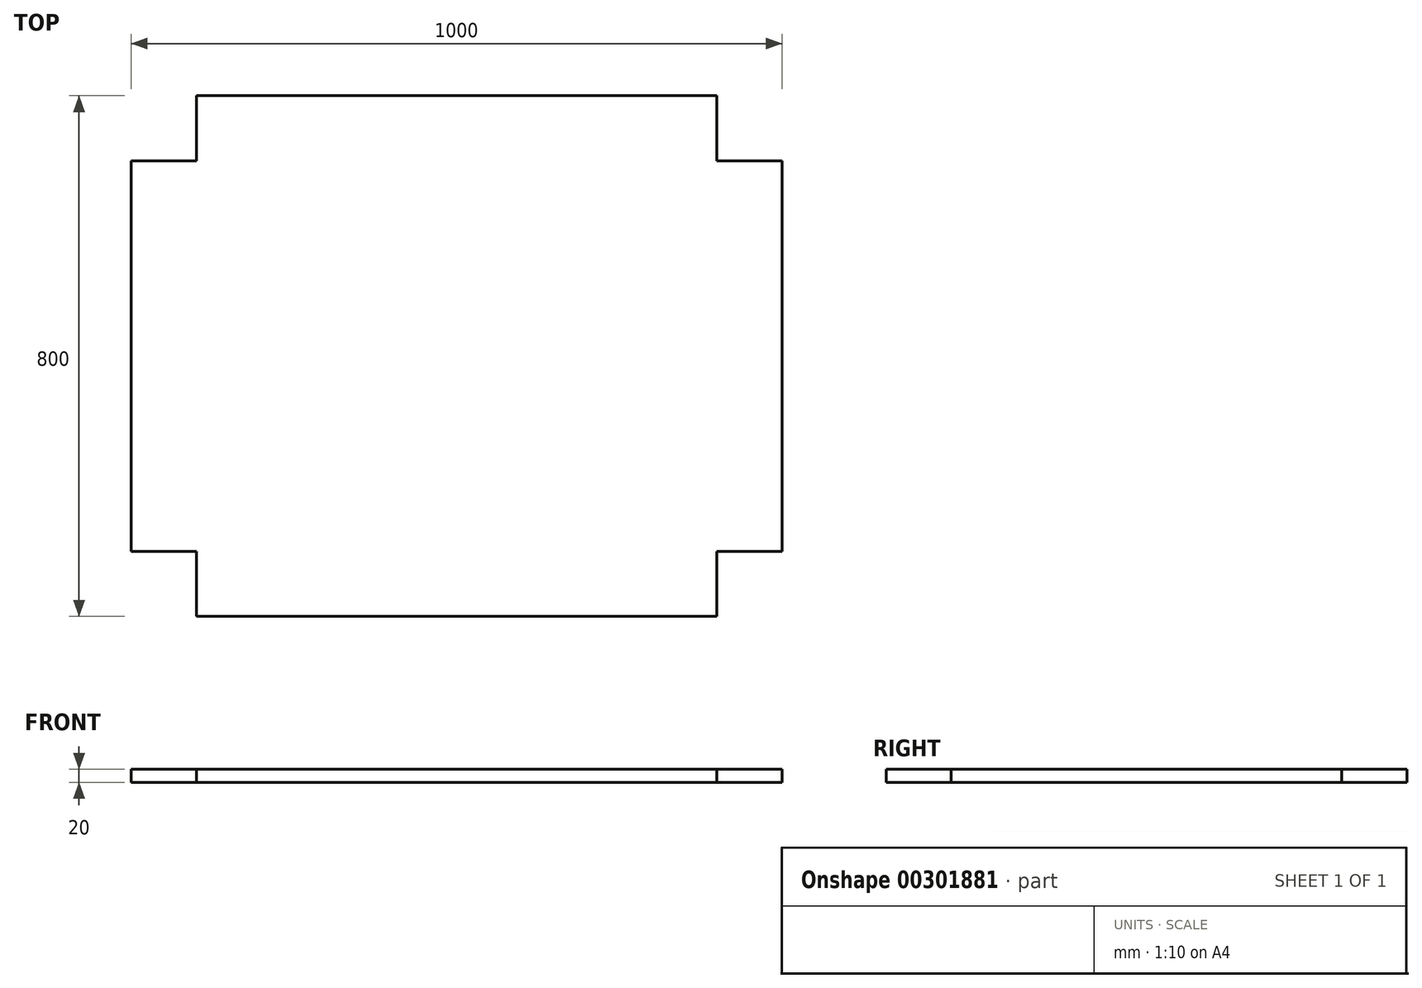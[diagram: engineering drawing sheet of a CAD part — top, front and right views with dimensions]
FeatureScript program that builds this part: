
annotation { "Feature Type Name" : "Feature", "Feature Type Description" : "" }
export const myFeature = defineFeature(function(context is Context, id is Id, definition is map)
    precondition{}
    {
        {
            var Q0;
            Q0=qCreatedBy(makeId("Top.planeOp"),FACE);
            var sketch = newSketch(context, id + "F0", { "sketchPlane" : qUnion([Q0])});
            skLineSegment(sketch, "E0", {"start": v(0, 0) * mm, "end": v(-1000, 0) * mm});
            skLineSegment(sketch, "E1", {"start": v(-1000, 0) * mm, "end": v(-1000, 6000) * mm});
            skLineSegment(sketch, "E2", {"start": v(-1000, 6000) * mm, "end": v(0, 6000) * mm});
            skLineSegment(sketch, "E3", {"start": v(0, 6000) * mm, "end": v(0, 7000) * mm});
            skLineSegment(sketch, "E4", {"start": v(0, 7000) * mm, "end": v(8000, 7000) * mm});
            skLineSegment(sketch, "E5", {"start": v(8000, 7000) * mm, "end": v(8000, 6000) * mm});
            skLineSegment(sketch, "E6", {"start": v(8000, 6000) * mm, "end": v(9000, 6000) * mm});
            skLineSegment(sketch, "E7", {"start": v(9000, 6000) * mm, "end": v(9000, 0) * mm});
            skLineSegment(sketch, "E8", {"start": v(9000, 0) * mm, "end": v(8000, 0) * mm});
            skLineSegment(sketch, "E9", {"start": v(8000, 0) * mm, "end": v(8000, -1000) * mm});
            skLineSegment(sketch, "E10", {"start": v(0, 0) * mm, "end": v(0, -1000) * mm});
            skLineSegment(sketch, "E11", {"start": v(0, -1000) * mm, "end": v(8000, -1000) * mm});
            skSolve(sketch);
        }
        {
            var Q0;
            Q0=makeQuery(id+"F0.imprint","IMPRINT",FACE,{"disambiguationData":[TD([[makeQuery(id+"F0.imprint","IMPRINT",EDGE,{"derivedFrom":sQuery(id+"F0.wireOp",EDGE,"E0")}),-1.0]])]});
            extrude(context, id + "F1", {"entities" : qUnion([Q0]), "depth" : 200 * mm});
        }
        {
            var Q0;
            Q0=makeQuery(id+"F1.opExtrude","SWEPT_BODY",BODY,{"disambiguationData":[OSD([sQuery(id+"F0.wireOp",EDGE,"E0"),sQuery(id+"F0.wireOp",EDGE,"E1"),sQuery(id+"F0.wireOp",EDGE,"E2"),sQuery(id+"F0.wireOp",EDGE,"E3"),sQuery(id+"F0.wireOp",EDGE,"E4"),sQuery(id+"F0.wireOp",EDGE,"E5"),sQuery(id+"F0.wireOp",EDGE,"E6"),sQuery(id+"F0.wireOp",EDGE,"E7"),sQuery(id+"F0.wireOp",EDGE,"E8"),sQuery(id+"F0.wireOp",EDGE,"E9"),sQuery(id+"F0.wireOp",EDGE,"E10"),sQuery(id+"F0.wireOp",EDGE,"E11")])]});
            var Q1;
            Q1=qCreatedBy(makeId("Origin.pointOp"),VERTEX);
            transform(context, id + "F2", {"entities" : qUnion([Q0]), "transformType" : TransformType.SCALE_UNIFORMLY, "scale" : 0.1, "scalePoint" : qUnion([Q1]), "makeCopy" : false});
        }
    });
